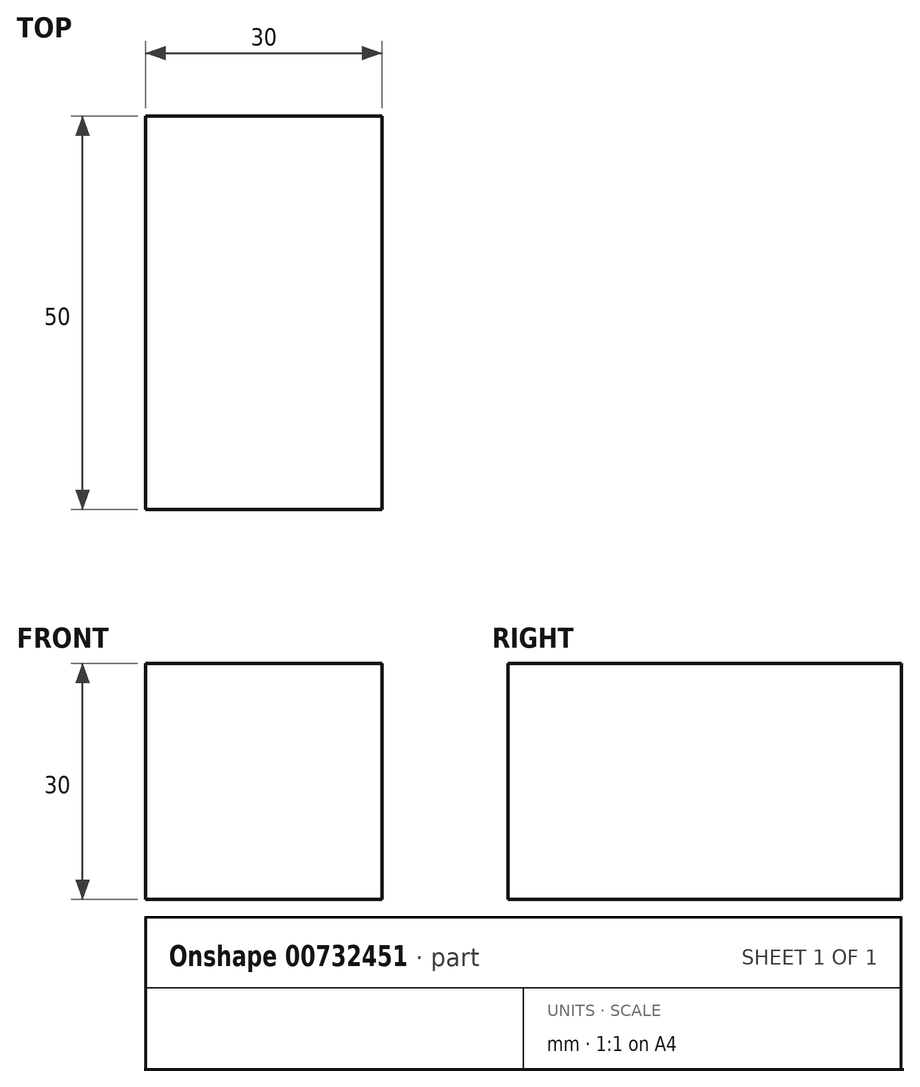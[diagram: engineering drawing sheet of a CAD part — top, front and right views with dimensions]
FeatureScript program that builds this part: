
annotation { "Feature Type Name" : "Feature", "Feature Type Description" : "" }
export const myFeature = defineFeature(function(context is Context, id is Id, definition is map)
    precondition{}
    {
        {
            var Q0;
            Q0=qCreatedBy(makeId("Front.planeOp"),FACE);
            var sketch = newSketch(context, id + "F0", { "sketchPlane" : qUnion([Q0])});
            skLineSegment(sketch, "E0.bottom", {"start": v(-16.16, -15.85) * mm, "end": v(13.84, -15.85) * mm});
            skLineSegment(sketch, "E0.top", {"start": v(-16.16, 14.15) * mm, "end": v(13.84, 14.15) * mm});
            skLineSegment(sketch, "E0.left", {"start": v(-16.16, -15.85) * mm, "end": v(-16.16, 14.15) * mm});
            skLineSegment(sketch, "E0.right", {"start": v(13.84, -15.85) * mm, "end": v(13.84, 14.15) * mm});
            skPoint(sketch, "E0.middle", {"position": v(-1.16, -0.85) * mm});
            skCircle(sketch, "E1", {"center": v(-1.16, -0.85) * mm, "radius": 3 * mm});
            skCircle(sketch, "E2", {"center": v(-1.16, -0.85) * mm, "radius": 3.5 * mm});
            skArc(sketch, "E3", {"start": v(-8.2, 3.44) * mm, "mid": v(-5.38, 3.42) * mm, "end": v(-5.36, 6.25) * mm});
            skArc(sketch, "E4", {"start": v(-10.97, 11.95) * mm, "mid": v(-13.8, 11.97) * mm, "end": v(-13.82, 9.14) * mm});
            skLineSegment(sketch, "E5", {"start": v(-13.82, 9.14) * mm, "end": v(-8.2, 3.44) * mm});
            skLineSegment(sketch, "E6", {"start": v(-5.36, 6.25) * mm, "end": v(-10.97, 11.95) * mm});
            skArc(sketch, "E7.MirrorCS", {"start": v(8.65, 11.95) * mm, "mid": v(11.48, 11.97) * mm, "end": v(11.5, 9.14) * mm});
            skLineSegment(sketch, "E8.MirrorCS", {"start": v(11.5, 9.14) * mm, "end": v(5.88, 3.44) * mm});
            skLineSegment(sketch, "E9.MirrorCS", {"start": v(3.03, 6.25) * mm, "end": v(8.65, 11.95) * mm});
            skArc(sketch, "E10.MirrorCS", {"start": v(5.88, 3.44) * mm, "mid": v(3.05, 3.42) * mm, "end": v(3.03, 6.25) * mm});
            skArc(sketch, "E11.MirrorCS", {"start": v(-8.2, -5.14) * mm, "mid": v(-5.38, -5.12) * mm, "end": v(-5.36, -7.95) * mm});
            skLineSegment(sketch, "E12.MirrorCS", {"start": v(-13.82, -10.84) * mm, "end": v(-8.2, -5.14) * mm});
            skArc(sketch, "E13.MirrorCS", {"start": v(-10.97, -13.64) * mm, "mid": v(-13.8, -13.66) * mm, "end": v(-13.82, -10.84) * mm});
            skLineSegment(sketch, "E14.MirrorCS", {"start": v(-5.36, -7.95) * mm, "end": v(-10.97, -13.64) * mm});
            skArc(sketch, "E15.MirrorCS", {"start": v(5.88, -5.14) * mm, "mid": v(3.05, -5.12) * mm, "end": v(3.03, -7.95) * mm});
            skLineSegment(sketch, "E16.MirrorCS", {"start": v(11.5, -10.84) * mm, "end": v(5.88, -5.14) * mm});
            skLineSegment(sketch, "E17.MirrorCS", {"start": v(3.03, -7.95) * mm, "end": v(8.65, -13.64) * mm});
            skArc(sketch, "E18.MirrorCS", {"start": v(8.65, -13.64) * mm, "mid": v(11.48, -13.66) * mm, "end": v(11.5, -10.84) * mm});
            skSolve(sketch);
        }
        {
            var Q0;
            Q0=makeQuery(id+"F0.imprint","IMPRINT",FACE,{"disambiguationData":[TD([[makeQuery(id+"F0.imprint","IMPRINT",EDGE,{"derivedFrom":sQuery(id+"F0.wireOp",EDGE,"E1")}),-1.0]])]});
            var Q1;
            Q1=makeQuery(id+"F0.imprint","IMPRINT",FACE,{"disambiguationData":[TD([[makeQuery(id+"F0.imprint","IMPRINT",EDGE,{"derivedFrom":sQuery(id+"F0.wireOp",EDGE,"E15.MirrorCS")}),1.0]])]});
            var Q2;
            Q2=makeQuery(id+"F0.imprint","IMPRINT",FACE,{"disambiguationData":[TD([[makeQuery(id+"F0.imprint","IMPRINT",EDGE,{"derivedFrom":sQuery(id+"F0.wireOp",EDGE,"E9.MirrorCS")}),-1.0]])]});
            var Q3;
            Q3=makeQuery(id+"F0.imprint","IMPRINT",FACE,{"disambiguationData":[TD([[makeQuery(id+"F0.imprint","IMPRINT",EDGE,{"derivedFrom":sQuery(id+"F0.wireOp",EDGE,"E3")}),1.0]])]});
            var Q4;
            Q4=makeQuery(id+"F0.imprint","IMPRINT",FACE,{"disambiguationData":[TD([[makeQuery(id+"F0.imprint","IMPRINT",EDGE,{"derivedFrom":sQuery(id+"F0.wireOp",EDGE,"E1")}),1.0]])]});
            var Q5;
            Q5=makeQuery(id+"F0.imprint","IMPRINT",FACE,{"disambiguationData":[TD([[makeQuery(id+"F0.imprint","IMPRINT",EDGE,{"derivedFrom":sQuery(id+"F0.wireOp",EDGE,"E12.MirrorCS")}),-1.0]])]});
            var Q6;
            Q6=makeQuery(id+"F0.imprint","IMPRINT",FACE,{"disambiguationData":[TD([[makeQuery(id+"F0.imprint","IMPRINT",EDGE,{"derivedFrom":sQuery(id+"F0.wireOp",EDGE,"E0.bottom")}),1.0]])]});
            extrude(context, id + "F1", {"entities" : qUnion([Q0, Q1, Q2, Q3, Q4, Q5, Q6]), "depth" : 50 * mm, "offsetDistance" : 25 * mm});
        }
    });
